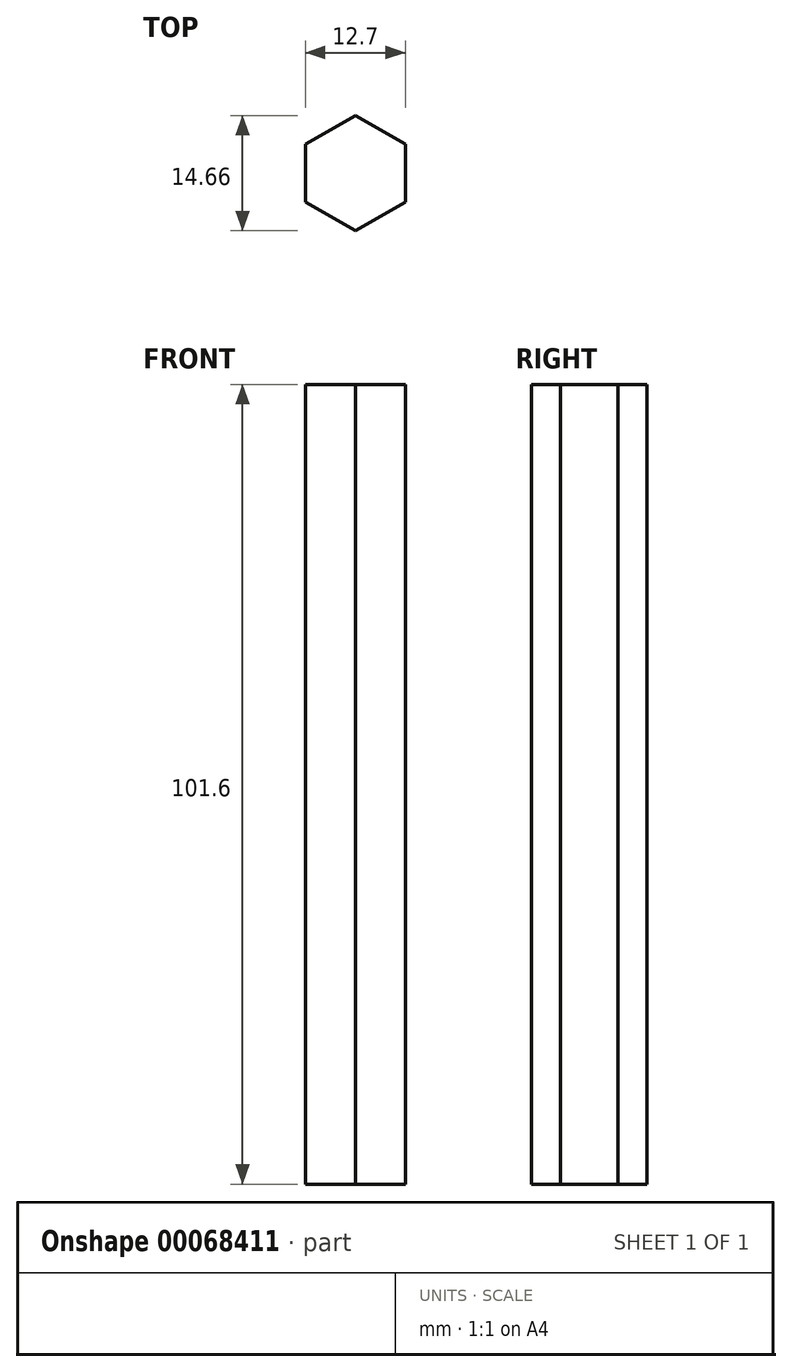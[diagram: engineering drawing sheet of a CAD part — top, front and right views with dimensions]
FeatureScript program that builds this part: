
annotation { "Feature Type Name" : "Feature", "Feature Type Description" : "" }
export const myFeature = defineFeature(function(context is Context, id is Id, definition is map)
    precondition{}
    {
        {
            var Q0;
            Q0=qCreatedBy(makeId("Top.planeOp"),FACE);
            var sketch = newSketch(context, id + "F0", { "sketchPlane" : qUnion([Q0])});
            skCircle(sketch, "E0.cCircle", {"center": v(0, 0) * mm, "radius": 6.35 * mm, "construction": true});
            skLineSegment(sketch, "E0.0", {"start": v(6.35, 3.67) * mm, "end": v(6.35, -3.67) * mm});
            skLineSegment(sketch, "E0.1", {"start": v(6.35, -3.67) * mm, "end": v(0, -7.33) * mm});
            skLineSegment(sketch, "E0.2", {"start": v(0, -7.33) * mm, "end": v(-6.35, -3.67) * mm});
            skLineSegment(sketch, "E0.3", {"start": v(-6.35, -3.67) * mm, "end": v(-6.35, 3.67) * mm});
            skLineSegment(sketch, "E0.4", {"start": v(-6.35, 3.67) * mm, "end": v(0, 7.33) * mm});
            skLineSegment(sketch, "E0.5", {"start": v(0, 7.33) * mm, "end": v(6.35, 3.67) * mm});
            skPoint(sketch, "E0.0.midPoint", {"position": v(6.35, 0) * mm});
            skSolve(sketch);
        }
        {
            var Q0;
            Q0=makeQuery(id+"F0.imprint","IMPRINT",FACE,{"disambiguationData":[TD([[makeQuery(id+"F0.imprint","IMPRINT",EDGE,{"derivedFrom":sQuery(id+"F0.wireOp",EDGE,"E0.0")}),-1.0]])]});
            extrude(context, id + "F1", {"entities" : qUnion([Q0]), "depth" : 101.6 * mm});
        }
    });
